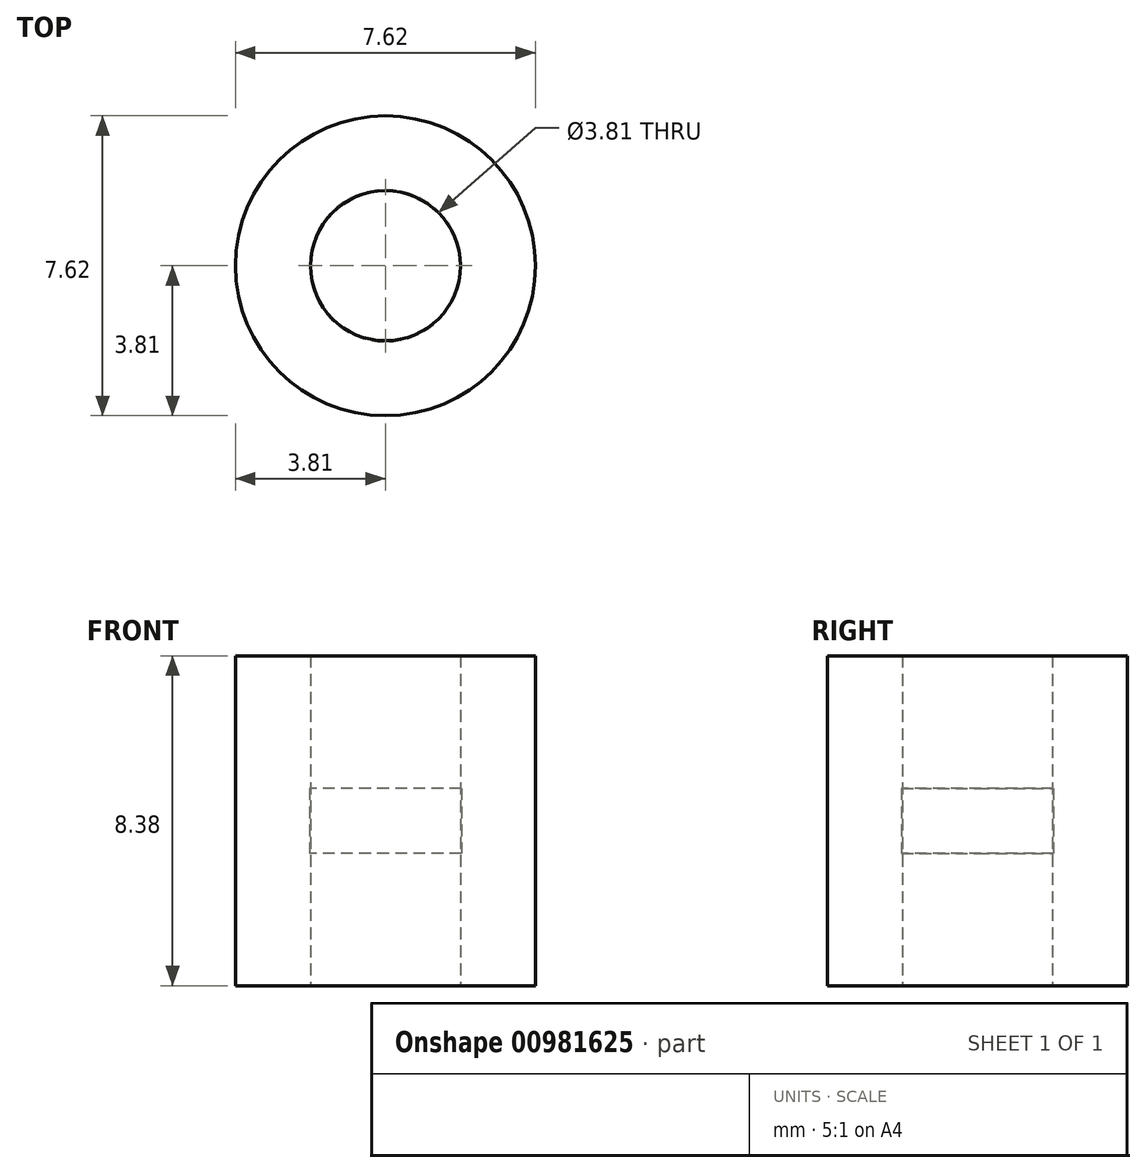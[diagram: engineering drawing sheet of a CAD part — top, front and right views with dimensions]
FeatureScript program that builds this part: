
annotation { "Feature Type Name" : "Feature", "Feature Type Description" : "" }
export const myFeature = defineFeature(function(context is Context, id is Id, definition is map)
    precondition{}
    {
        {
            var Q0;
            Q0=qCreatedBy(makeId("Top.planeOp"),FACE);
            var sketch = newSketch(context, id + "F0", { "sketchPlane" : qUnion([Q0])});
            skCircle(sketch, "E0", {"center": v(0, 0) * mm, "radius": 3.81 * mm});
            skCircle(sketch, "E1", {"center": v(0, 0) * mm, "radius": 1.9 * mm});
            skSolve(sketch);
        }
        {
            var Q0;
            Q0 = qSketchRegion(id + "F0", true);
            extrude(context, id + "F1", {"entities" : qUnion([Q0]), "endBound" : BoundingType.SYMMETRIC, "depth" : 8.38 * mm, "offsetDistance" : 25.4 * mm});
        }
        {
            var Q0;
            Q0=qCreatedBy(makeId("Top.planeOp"),FACE);
            var sketch = newSketch(context, id + "F2", { "sketchPlane" : qUnion([Q0])});
            skCircle(sketch, "E2", {"center": v(0, 0) * mm, "radius": 1.93 * mm});
            skSolve(sketch);
        }
        {
            var Q0;
            Q0 = qSketchRegion(id + "F2", true);
            extrude(context, id + "F3", {"entities" : qUnion([Q0]), "endBound" : BoundingType.SYMMETRIC, "depth" : 1.65 * mm, "offsetDistance" : 25.4 * mm});
        }
    });
